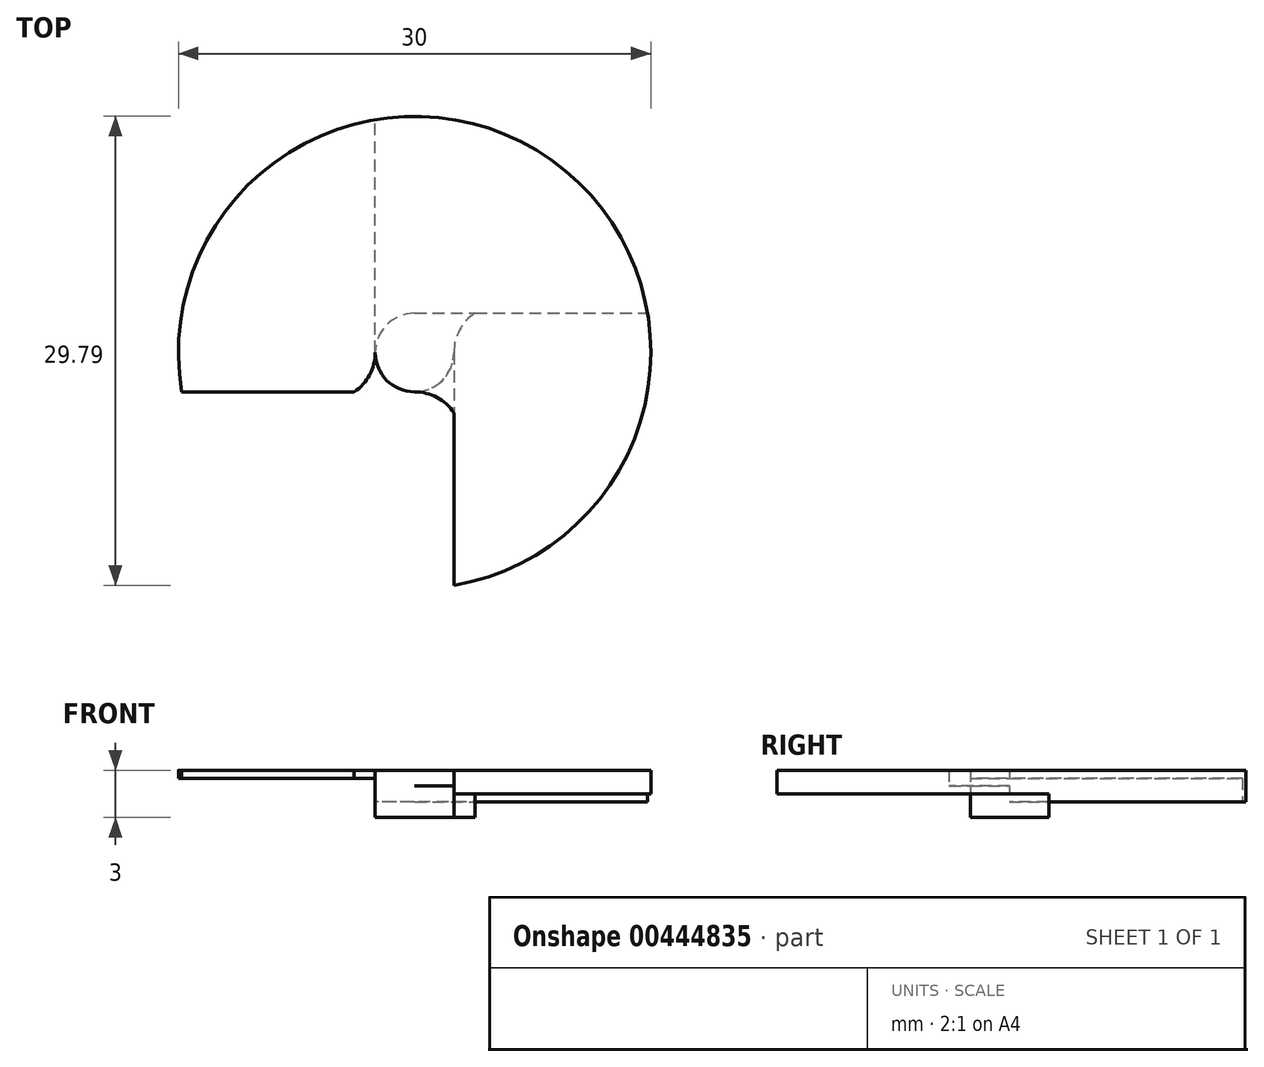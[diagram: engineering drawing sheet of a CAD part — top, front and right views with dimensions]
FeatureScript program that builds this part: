
annotation { "Feature Type Name" : "Feature", "Feature Type Description" : "" }
export const myFeature = defineFeature(function(context is Context, id is Id, definition is map)
    precondition{}
    {
        {
            var Q0;
            Q0=qCreatedBy(makeId("Top.planeOp"),FACE);
            var sketch = newSketch(context, id + "F0", { "sketchPlane" : qUnion([Q0])});
            skCircle(sketch, "E0", {"center": v(0, 0) * mm, "radius": 15 * mm});
            skCircle(sketch, "E1", {"center": v(0, 0) * mm, "radius": 2.5 * mm});
            skLineSegment(sketch, "E2", {"start": v(-2.5, 0) * mm, "end": v(-2.5, 14.8) * mm});
            skLineSegment(sketch, "E3", {"start": v(0, 2.5) * mm, "end": v(14.8, 2.5) * mm});
            skLineSegment(sketch, "E4", {"start": v(2.5, 0) * mm, "end": v(2.5, -14.8) * mm});
            skLineSegment(sketch, "E5", {"start": v(0, -2.5) * mm, "end": v(-14.8, -2.5) * mm});
            skArc(sketch, "E6", {"start": v(2.5, 0) * mm, "mid": v(2.86, 1.42) * mm, "end": v(3.84, 2.5) * mm});
            skArc(sketch, "E7", {"start": v(0, -2.5) * mm, "mid": v(1.42, -2.86) * mm, "end": v(2.5, -3.84) * mm});
            skArc(sketch, "E8", {"start": v(-2.5, 0) * mm, "mid": v(-2.86, -1.42) * mm, "end": v(-3.84, -2.5) * mm});
            skSolve(sketch);
        }
        {
            var Q0;
            {var subQ0=sQuery(id+"F0.wireOp",EDGE,"E1");var subQ1=makeQuery(id+"F0.imprint","INTERSECT",VERTEX,{"derivedFrom":[subQ0,sQuery(id+"F0.wireOp",EDGE,"E3")]});Q0=makeQuery(id+"F0.imprint","IMPRINT",FACE,{"disambiguationData":[TD([[makeQuery(id+"F0.imprint","IMPRINT",EDGE,{"disambiguationData":[TD([[subQ1,1.0]])],"derivedFrom":subQ0}),1.0]])]});}
            var Q1;
            {var subQ0=sQuery(id+"F0.wireOp",EDGE,"E2");Q1=makeQuery(id+"F0.imprint","IMPRINT",FACE,{"disambiguationData":[TD([[makeQuery(id+"F0.imprint","IMPRINT",EDGE,{"derivedFrom":subQ0}),1.0]])]});}
            var Q2;
            {var subQ0=sQuery(id+"F0.wireOp",EDGE,"E2");Q2=makeQuery(id+"F0.imprint","IMPRINT",FACE,{"disambiguationData":[TD([[makeQuery(id+"F0.imprint","IMPRINT",EDGE,{"derivedFrom":subQ0}),-1.0]])]});}
            var Q3;
            {var subQ0=sQuery(id+"F0.wireOp",EDGE,"E3");Q3=makeQuery(id+"F0.imprint","IMPRINT",FACE,{"disambiguationData":[TD([[makeQuery(id+"F0.imprint","IMPRINT",EDGE,{"derivedFrom":subQ0}),-1.0]])]});}
            var Q4;
            {var subQ0=sQuery(id+"F0.wireOp",EDGE,"E4");Q4=makeQuery(id+"F0.imprint","IMPRINT",FACE,{"disambiguationData":[TD([[makeQuery(id+"F0.imprint","IMPRINT",EDGE,{"derivedFrom":subQ0}),-1.0]])]});}
            var Q5;
            {var subQ3=sQuery(id+"F0.wireOp",EDGE,"E4");Q5=makeQuery(id+"F0.imprint","IMPRINT",FACE,{"disambiguationData":[TD([[makeQuery(id+"F0.imprint","IMPRINT",EDGE,{"derivedFrom":subQ3}),1.0]])]});}
            var Q6;
            {var subQ4=sQuery(id+"F0.wireOp",EDGE,"E7");Q6=makeQuery(id+"F0.imprint","IMPRINT",FACE,{"disambiguationData":[TD([[makeQuery(id+"F0.imprint","IMPRINT",EDGE,{"derivedFrom":subQ4}),-1.0]])]});}
            var Q7;
            {var subQ0=sQuery(id+"F0.wireOp",EDGE,"E8");Q7=makeQuery(id+"F0.imprint","IMPRINT",FACE,{"disambiguationData":[TD([[makeQuery(id+"F0.imprint","IMPRINT",EDGE,{"derivedFrom":subQ0}),1.0]])]});}
            extrude(context, id + "F1", {"entities" : qUnion([Q0, Q1, Q2, Q3, Q4, Q5, Q6, Q7]), "depth" : 3 * mm});
        }
        {
            var Q0;
            {var subQ0=sQuery(id+"F0.wireOp",EDGE,"E2");Q0=makeQuery(id+"F0.imprint","IMPRINT",FACE,{"disambiguationData":[TD([[makeQuery(id+"F0.imprint","IMPRINT",EDGE,{"derivedFrom":subQ0}),1.0]])]});}
            extrude(context, id + "F2", {"entities" : qUnion([Q0]), "operationType" : NewBodyOperationType.REMOVE, "depth" : 2.5 * mm});
        }
        {
            var Q0;
            {var subQ4=sQuery(id+"F0.wireOp",EDGE,"E7");Q0=makeQuery(id+"F0.imprint","IMPRINT",FACE,{"disambiguationData":[TD([[makeQuery(id+"F0.imprint","IMPRINT",EDGE,{"derivedFrom":subQ4}),-1.0]])]});}
            var Q1;
            {var subQ0=sQuery(id+"F0.wireOp",EDGE,"E8");Q1=makeQuery(id+"F0.imprint","IMPRINT",FACE,{"disambiguationData":[TD([[makeQuery(id+"F0.imprint","IMPRINT",EDGE,{"derivedFrom":subQ0}),1.0]])]});}
            extrude(context, id + "F3", {"entities" : qUnion([Q0, Q1]), "operationType" : NewBodyOperationType.REMOVE, "depth" : 2 * mm});
        }
        {
            var Q0;
            {var subQ3=sQuery(id+"F0.wireOp",EDGE,"E4");Q0=makeQuery(id+"F0.imprint","IMPRINT",FACE,{"disambiguationData":[TD([[makeQuery(id+"F0.imprint","IMPRINT",EDGE,{"derivedFrom":subQ3}),1.0]])]});}
            var Q1;
            {var subQ3=sQuery(id+"F0.wireOp",EDGE,"E7");Q1=makeQuery(id+"F0.imprint","IMPRINT",FACE,{"disambiguationData":[TD([[makeQuery(id+"F0.imprint","IMPRINT",EDGE,{"derivedFrom":subQ3}),1.0]])]});}
            extrude(context, id + "F4", {"entities" : qUnion([Q0, Q1]), "operationType" : NewBodyOperationType.REMOVE, "depth" : 1.5 * mm});
        }
        {
            var Q0;
            {var subQ0=sQuery(id+"F0.wireOp",EDGE,"E2");Q0=makeQuery(id+"F0.imprint","IMPRINT",FACE,{"disambiguationData":[TD([[makeQuery(id+"F0.imprint","IMPRINT",EDGE,{"derivedFrom":subQ0}),-1.0]])]});}
            var Q1;
            {var subQ3=sQuery(id+"F0.wireOp",EDGE,"E6");Q1=makeQuery(id+"F0.imprint","IMPRINT",FACE,{"disambiguationData":[TD([[makeQuery(id+"F0.imprint","IMPRINT",EDGE,{"derivedFrom":subQ3}),1.0]])]});}
            extrude(context, id + "F5", {"entities" : qUnion([Q0, Q1]), "operationType" : NewBodyOperationType.REMOVE, "depth" : 1 * mm});
        }
    });
